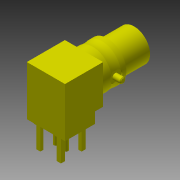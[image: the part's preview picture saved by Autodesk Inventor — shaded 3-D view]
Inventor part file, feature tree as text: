
AUTODESK INVENTOR PART (.ipt)
format: ipt  version: 2014 SP2 (Build 180246200, 246)  size: 276,480 bytes
history: native  units: mm
features: sketch x11, extrude x8, other x7, revolve x4
ambient origin geometry x8: Origin, YZ Plane, XZ Plane, XY Plane, X Axis, Y Axis, Z Axis, Center Point
bodies: Solid1 (feature_tree)
feature tree (30):
  extrude  "Extrusion1"  Depth=2.7mm TaperAngle=0.0deg
  extrude  "Extrusion2"  Depth=2.71035mm TaperAngle=0.0deg
  extrude  "Extrusion3"  TaperAngle=360.0deg  [1 undecoded]
  extrude  "Extrusion4"  Depth=0.15mm TaperAngle=0.0deg
  extrude  "Extrusion5"  TaperAngle=360.0deg  [1 undecoded]
  revolve  "Revolution1"  Angle=360.0deg
  extrude  "Extrusion6"  [1 undecoded]
  extrude  "Extrusion7"  [1 undecoded]
  extrude  "Extrusion8"  [1 undecoded]
  revolve  "Revolution2"  [1 undecoded]
  revolve  "Revolution3"  [1 undecoded]
  revolve  "Revolution4"  [1 undecoded]
  other  "fh1_XY"
  other  "fh1_YZ"
  other  "fh1_ZX"
  other  "fh1_X"
  other  "fh1_Y"
  other  "fh1_Z"
  other  "fh1_Center"
  sketch  "Sketch0"  dims[d0=4.7mm d1=0.0mm d2=2.7mm d3=0.0mm]
  sketch  "Sketch2"  dims[d4=2.95mm d5=0.0mm d6=2.71035mm d7=0.0mm]
  sketch  "Sketch3"  dims[d8=2.71035mm d9=0.0mm d10=360.0deg]
  sketch  "Sketch4"  dims[d11=3.0mm d12=0.0mm d13=0.15mm d14=0.0mm]
  sketch  "Sketch5"  dims[d15=0.15mm d16=0.0mm d17=360.0deg]
  sketch  "Sketch6"  dims[d18=360.0deg d19=360.0deg]
  sketch  "Sketch7"
  sketch  "Sketch8"
  sketch  "Sketch9"
  sketch  "Sketch10"
  sketch  "Sketch11"
note: 8 required parameter values undecoded (feature->parameter linkage not recoverable at this tier; creation-order binding heuristic only, values carry confidence <= 0.55)
